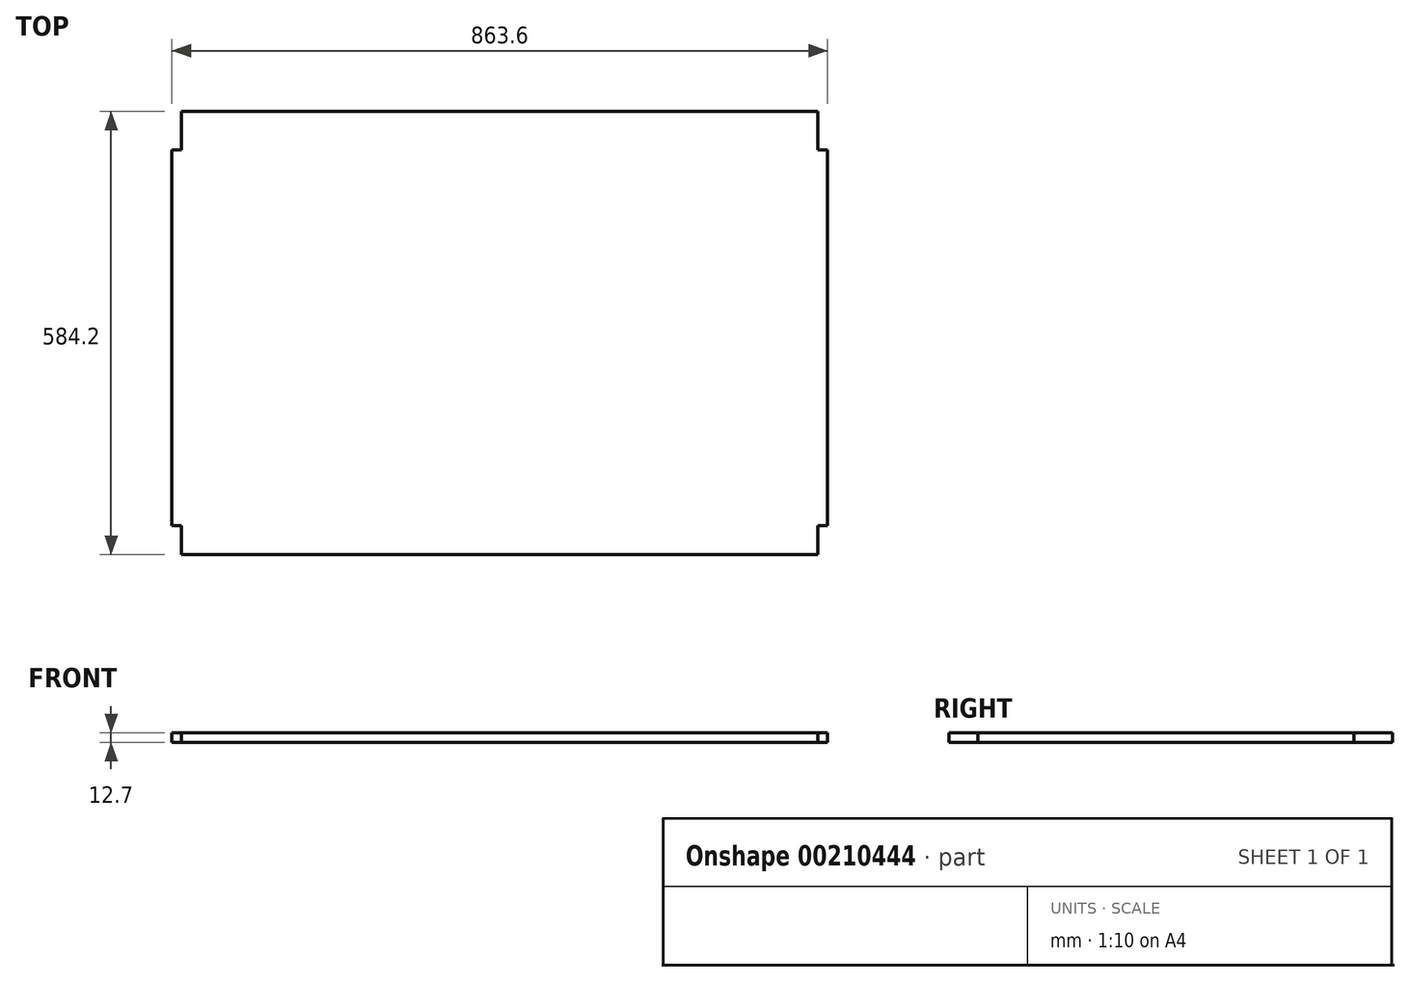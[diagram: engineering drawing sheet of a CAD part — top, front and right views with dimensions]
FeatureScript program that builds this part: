
annotation { "Feature Type Name" : "Feature", "Feature Type Description" : "" }
export const myFeature = defineFeature(function(context is Context, id is Id, definition is map)
    precondition{}
    {
        {
            var Q0;
            Q0=qCreatedBy(makeId("Top.planeOp"),FACE);
            var sketch = newSketch(context, id + "F0", { "sketchPlane" : qUnion([Q0])});
            skLineSegment(sketch, "E0.bottom", {"start": v(419.1, 292.1) * mm, "end": v(-419.1, 292.1) * mm});
            skLineSegment(sketch, "E0.top", {"start": v(419.1, -292.1) * mm, "end": v(-419.1, -292.1) * mm});
            skLineSegment(sketch, "E0.left", {"start": v(431.8, 241.3) * mm, "end": v(431.8, -254) * mm});
            skLineSegment(sketch, "E0.right", {"start": v(-431.8, 241.3) * mm, "end": v(-431.8, -254) * mm});
            skPoint(sketch, "E0.middle", {"position": v(0, 0) * mm});
            skLineSegment(sketch, "E1", {"start": v(-419.1, 292.1) * mm, "end": v(-419.1, 241.3) * mm});
            skLineSegment(sketch, "E2", {"start": v(-419.1, 241.3) * mm, "end": v(-431.8, 241.3) * mm});
            skLineSegment(sketch, "E3", {"start": v(-431.8, -254) * mm, "end": v(-419.1, -254) * mm});
            skLineSegment(sketch, "E4", {"start": v(419.1, -254) * mm, "end": v(431.8, -254) * mm});
            skLineSegment(sketch, "E5", {"start": v(431.8, 241.3) * mm, "end": v(419.1, 241.3) * mm});
            skLineSegment(sketch, "E6", {"start": v(-419.1, -254) * mm, "end": v(-419.1, -292.1) * mm});
            skLineSegment(sketch, "E7", {"start": v(419.1, -254) * mm, "end": v(419.1, -292.1) * mm});
            skLineSegment(sketch, "E8", {"start": v(419.1, 292.1) * mm, "end": v(419.1, 241.3) * mm});
            skPoint(sketch, "E9.orphan", {"position": v(-431.8, 292.1) * mm});
            skPoint(sketch, "E10.orphan", {"position": v(431.8, 292.1) * mm});
            skPoint(sketch, "E11.orphan", {"position": v(431.8, -292.1) * mm});
            skPoint(sketch, "E12.orphan", {"position": v(-431.8, -292.1) * mm});
            skSolve(sketch);
        }
        {
            var Q0;
            Q0 = qSketchRegion(id + "F0", true);
            extrude(context, id + "F1", {"entities" : qUnion([Q0]), "depth" : 12.7 * mm});
        }
    });
